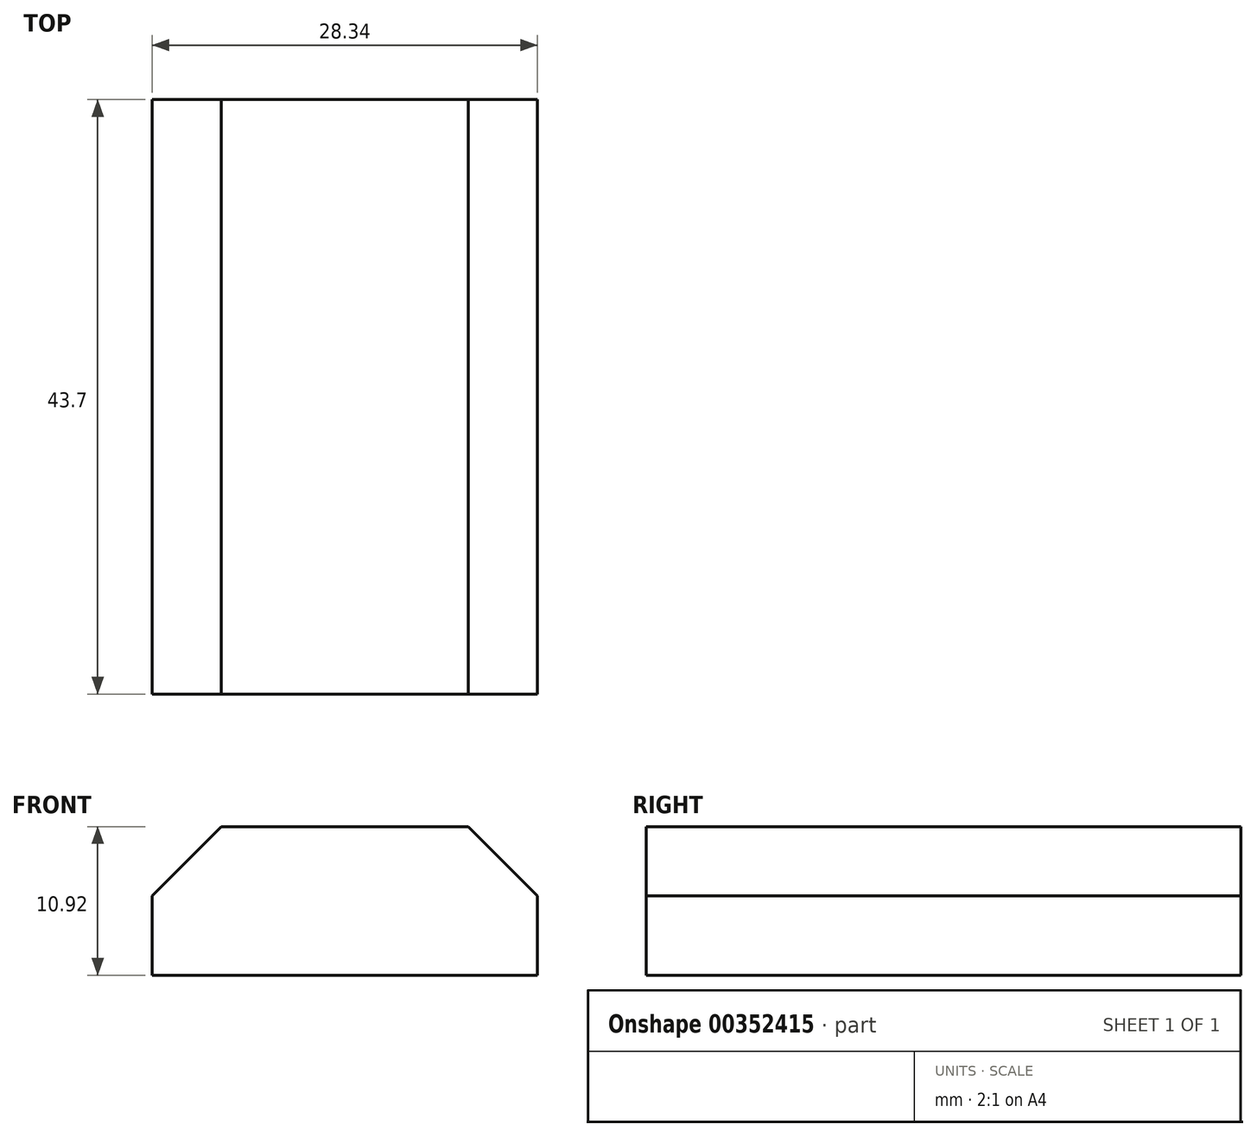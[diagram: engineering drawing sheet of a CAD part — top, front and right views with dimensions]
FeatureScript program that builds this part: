
annotation { "Feature Type Name" : "Feature", "Feature Type Description" : "" }
export const myFeature = defineFeature(function(context is Context, id is Id, definition is map)
    precondition{}
    {
        {
            var Q0;
            Q0=qCreatedBy(makeId("Top.planeOp"),FACE);
            var sketch = newSketch(context, id + "F0", { "sketchPlane" : qUnion([Q0])});
            skLineSegment(sketch, "E0.bottom", {"start": v(14.17, 21.85) * mm, "end": v(-14.17, 21.85) * mm});
            skLineSegment(sketch, "E0.top", {"start": v(14.17, -21.85) * mm, "end": v(-14.17, -21.85) * mm});
            skLineSegment(sketch, "E0.left", {"start": v(14.17, 21.85) * mm, "end": v(14.17, -21.85) * mm});
            skLineSegment(sketch, "E0.right", {"start": v(-14.17, 21.85) * mm, "end": v(-14.17, -21.85) * mm});
            skPoint(sketch, "E0.middle", {"position": v(0, 0) * mm});
            skSolve(sketch);
        }
        {
            var Q0;
            Q0=makeQuery(id+"F0.imprint","IMPRINT",FACE,{"disambiguationData":[TD([[makeQuery(id+"F0.imprint","IMPRINT",EDGE,{"derivedFrom":sQuery(id+"F0.wireOp",EDGE,"E0.bottom")}),1.0]])]});
            extrude(context, id + "F1", {"entities" : qUnion([Q0]), "depth" : 10.92 * mm});
        }
        {
            var Q0;
            Q0=makeQuery(id+"F1.opExtrude","CAP_EDGE",EDGE,{"disambiguationData":[OSD([sQuery(id+"F0.wireOp",EDGE,"E0.right")])],"isStart":false});
            var Q1;
            Q1=makeQuery(id+"F1.opExtrude","CAP_EDGE",EDGE,{"disambiguationData":[OSD([sQuery(id+"F0.wireOp",EDGE,"E0.left")])],"isStart":false});
            chamfer(context, id + "F2", {"entities" : qUnion([Q0, Q1]), "width" : 5.08 * mm, "tangentPropagation" : true});
        }
    });
